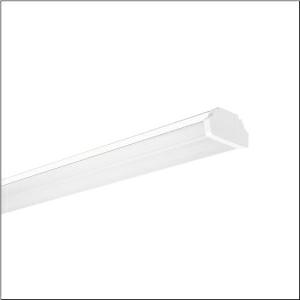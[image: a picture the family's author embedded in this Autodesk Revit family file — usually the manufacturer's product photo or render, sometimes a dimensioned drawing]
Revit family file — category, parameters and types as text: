
# Revit family: modario_31_gen_2_53bm812cv475c2_71b4
name_source: partatom
category: Lighting Fixtures
units: mm (PartAtom-declared; Revit-internal decimal feet)

## family parameters
Cut with Voids When Loaded = No
Host = Face
Light Source = No
Part Type = Normal
Room Calculation Point = No
Round Connector Dimension = Use Diameter
Shared = No

## types (1)
- --- (1 x LED, 7600 lm, 40.5 W, 4000K)
    Apparent Load = 41 VA
    CIE Flux Codes = 47 80 95 93 100
    Color Rendering = 80
    Color Temperature = 4000K
    Default Elevation = 1800 mm
    Description = Modario 31 Gen.2, luminaire insert, of sheet steel, coil coated, white, length: 1.495mm, width: 81mm, height: 82mm, 5x system unit, system units: 299mm, LED rated luminous flux: 7.600lm, light colour: 840, SDCM (Standard Deviation of Colour Matching)MacAdam ≤ 3 SDCM (initial), control gear: ON/OFF Multilumen, CLOi, with plug, 3-pole, with phase selection, mains connection: 220..240V, AC, 50/60Hz, start of lifetime: 41W, end of service life: 48W, through-wiring accessed according to module size, primary optical cover: cover, of PMMA, light emission: direct distribution, primary light characteristic: symmetric, protection rating (complete): IP20, protection rating (LED compartment): IP50, insulation class (complete): insulation class I (protective earthing), certification: CE, ENEC, VDE, UKCA, impact resistance: IK03, permissible ambient temperature for indoor applications: -35..+50°C, corresponds to IFS (International Featured Standards) requirements for safety and quality in the food industry, reducing of maximum allowable ambient temperature of 5°C with ceiling mounting, IP40 when using the optional accessory 5TP9018, packaging unit: 1 piece
    Height = 92 mm
    Lamp = 1 x LED
    Lamp Light Flux = 7600 lm
    Lamp Power = 40.5 W
    Lamp count = 1
    Length = 1495 mm
    Luminous efficacy = 188 lm/W
    Manufacturer = Siteco
    ModVariant = No
    Model = 53BM812CV475C2
    Mounting Place = Ceiling
    Mounting Type = Pendant
    Number of Poles = 1
    OnlyDefault = Yes
    Power Factor = 1
    Product Name = Modario 31 Gen.2
    Product group = luminaire insert | ceiling pendant
    ProductGroupID = 901
    Protection Class = Protection class I
    Protection Degree = IP 20
    RLX_Detail_Level = 1
    RLX_Emergency_Light_Flux = 0 lm
    RLX_Emergency_Type = 0
    RLX_Emergency_Type_DB = No
    RlxData = <blob elided: 39817 chars, md5=b79322bf>
    Socket = socket
    Standby Power = 0 W
    System Light Flux = 7600 lm
    System Power = 41 W
    Type Comments = factory setting: luminous flux: 100 % | (A | C | E) | 94 mA
    Type Image = l_1341886.jpg
    URL = http://relux.com
    VarID = @adj_042301
    Voltage = 0 V
    Weight = 0.00 kg
    Width = 81 mm

## geometry (parser evidence)
native form markers: Blend x4, Sweep x10
no freeform markers — native parametric forms only
